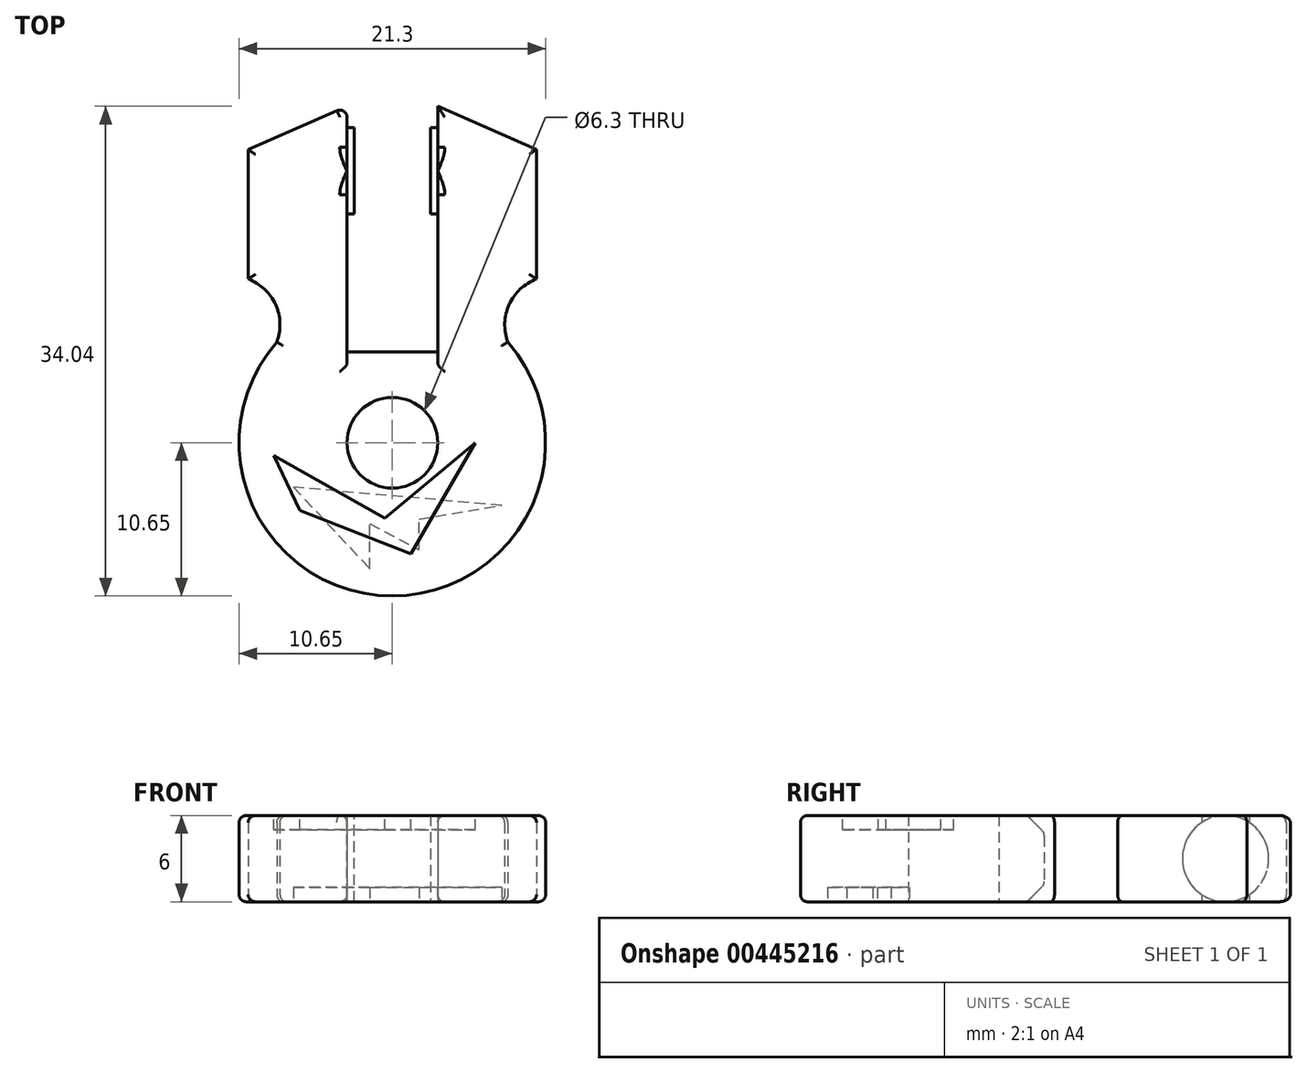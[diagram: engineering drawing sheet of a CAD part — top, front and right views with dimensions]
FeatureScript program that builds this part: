
annotation { "Feature Type Name" : "Feature", "Feature Type Description" : "" }
export const myFeature = defineFeature(function(context is Context, id is Id, definition is map)
    precondition{}
    {
        {
            var Q0;
            Q0=qCreatedBy(makeId("Top.planeOp"),FACE);
            var sketch = newSketch(context, id + "F0", { "sketchPlane" : qUnion([Q0])});
            skArc(sketch, "E0", {"start": v(-8.03, 7) * mm, "mid": v(0, -10.65) * mm, "end": v(8.03, 7) * mm});
            skCircle(sketch, "E1", {"center": v(0, 0) * mm, "radius": 3.15 * mm});
            skLineSegment(sketch, "E2", {"start": v(3.15, 10.17) * mm, "end": v(3.15, 23.39) * mm});
            skLineSegment(sketch, "E3", {"start": v(-3.15, 10.17) * mm, "end": v(-3.15, 23.39) * mm});
            skLineSegment(sketch, "E4", {"start": v(-3.15, 23.39) * mm, "end": v(-10.02, 20.38) * mm});
            skLineSegment(sketch, "E5.MirrorCS", {"start": v(3.15, 23.39) * mm, "end": v(10.02, 20.38) * mm});
            skLineSegment(sketch, "E6", {"start": v(-10.02, 20.38) * mm, "end": v(-10.02, 11.38) * mm});
            skLineSegment(sketch, "E7", {"start": v(10.02, 20.38) * mm, "end": v(10.02, 11.38) * mm});
            skLineSegment(sketch, "E8", {"start": v(-3.15, 23.39) * mm, "end": v(-3.15, 21.89) * mm});
            skLineSegment(sketch, "E9", {"start": v(-3.15, 21.89) * mm, "end": v(-2.65, 21.89) * mm});
            skLineSegment(sketch, "E10", {"start": v(-2.65, 21.89) * mm, "end": v(-2.65, 15.89) * mm});
            skLineSegment(sketch, "E11", {"start": v(-2.65, 15.89) * mm, "end": v(-3.15, 15.89) * mm});
            skLineSegment(sketch, "E12", {"start": v(-2.65, 18.89) * mm, "end": v(-3.15, 18.89) * mm});
            skLineSegment(sketch, "E13.MirrorCS", {"start": v(2.65, 21.89) * mm, "end": v(2.65, 15.89) * mm});
            skLineSegment(sketch, "E14.MirrorCS", {"start": v(2.65, 18.89) * mm, "end": v(3.15, 18.89) * mm});
            skLineSegment(sketch, "E15.MirrorCS", {"start": v(2.65, 15.89) * mm, "end": v(3.15, 15.89) * mm});
            skLineSegment(sketch, "E16.MirrorCS", {"start": v(3.15, 21.89) * mm, "end": v(2.65, 21.89) * mm});
            skPoint(sketch, "E17.orphan", {"position": v(6.63, 8.34) * mm});
            skArc(sketch, "E18.MirrorCS", {"start": v(-10.02, 11.38) * mm, "mid": v(-8.11, 9.6) * mm, "end": v(-8.03, 7) * mm});
            skPoint(sketch, "E19.orphan", {"position": v(-6.63, 8.34) * mm});
            skLineSegment(sketch, "E20", {"start": v(0, 6.3) * mm, "end": v(-3.15, 6.3) * mm});
            skLineSegment(sketch, "E21", {"start": v(-3.15, 6.3) * mm, "end": v(-3.15, 10.17) * mm});
            skLineSegment(sketch, "E22.MirrorCS", {"start": v(3.15, 6.3) * mm, "end": v(3.15, 10.17) * mm});
            skLineSegment(sketch, "E23.MirrorCS", {"start": v(0, 6.3) * mm, "end": v(3.15, 6.3) * mm});
            skArc(sketch, "E24.MirrorCS", {"start": v(10.02, 11.38) * mm, "mid": v(8.11, 9.6) * mm, "end": v(8.03, 7) * mm});
            skSolve(sketch);
        }
        {
            var Q0;
            Q0=makeQuery(id+"F0.imprint","IMPRINT",FACE,{"disambiguationData":[TD([[makeQuery(id+"F0.imprint","IMPRINT",EDGE,{"derivedFrom":sQuery(id+"F0.wireOp",EDGE,"E1")}),-1.0]])]});
            extrude(context, id + "F1", {"entities" : qUnion([Q0]), "depth" : 3 * mm, "hasSecondDirection" : true, "secondDirectionOppositeDirection" : true, "secondDirectionDepth" : 3 * mm});
        }
        {
            var Q0;
            Q0=makeQuery(id+"F1.opExtrude","SWEPT_FACE",FACE,{"disambiguationData":[OSD([sQuery(id+"F0.wireOp",EDGE,"E3"),sQuery(id+"F0.wireOp",EDGE,"E8"),sQuery(id+"F0.wireOp",EDGE,"E21")])]});
            var sketch = newSketch(context, id + "F2", { "sketchPlane" : qUnion([Q0])});
            skPoint(sketch, "E25.endSnap0", {"position": v(23.39, 0) * mm});
            skCircle(sketch, "E26", {"center": v(18.89, 0) * mm, "radius": 3 * mm});
            skSolve(sketch);
        }
        {
            var Q0;
            {var subQ0=sQuery(id+"F2.wireOp",EDGE,"E26");var subQ1=sQuery(id+"F0.wireOp",EDGE,"E21");var subQ2=sQuery(id+"F0.wireOp",EDGE,"E8");var subQ3=sQuery(id+"F0.wireOp",EDGE,"E3");var subQ4=makeQuery(id+"F2.imprint","INTERSECT",VERTEX,{"derivedFrom":[makeQuery(id+"F1.opExtrude","CAP_EDGE",EDGE,{"disambiguationData":[OSD([subQ3,subQ2,subQ1])],"isStart":true}),subQ0]});Q0=makeQuery(id+"F2.imprint","IMPRINT",FACE,{"disambiguationData":[TD([[makeQuery(id+"F2.imprint","IMPRINT",EDGE,{"disambiguationData":[TD([[subQ4,1.0]])],"derivedFrom":subQ0}),1.0]])]});}
            extrude(context, id + "F3", {"entities" : qUnion([Q0]), "operationType" : NewBodyOperationType.ADD, "depth" : .5 * mm});
        }
        {
            var Q0;
            Q0=makeQuery(id+"F1.opExtrude","SWEPT_FACE",FACE,{"disambiguationData":[OSD([sQuery(id+"F0.wireOp",EDGE,"E2"),sQuery(id+"F0.wireOp",EDGE,"E22.MirrorCS")])]});
            var sketch = newSketch(context, id + "F4", { "sketchPlane" : qUnion([Q0])});
            skPoint(sketch, "E27.endSnap0", {"position": v(-23.39, 0) * mm});
            skCircle(sketch, "E28", {"center": v(-18.89, 0) * mm, "radius": 3 * mm});
            skSolve(sketch);
        }
        {
            var Q0;
            {var subQ0=sQuery(id+"F4.wireOp",EDGE,"E28");var subQ1=sQuery(id+"F0.wireOp",EDGE,"E22.MirrorCS");var subQ2=sQuery(id+"F0.wireOp",EDGE,"E2");var subQ3=makeQuery(id+"F4.imprint","INTERSECT",VERTEX,{"derivedFrom":[makeQuery(id+"F1.opExtrude","CAP_EDGE",EDGE,{"disambiguationData":[OSD([subQ2,subQ1])],"isStart":true}),subQ0]});Q0=makeQuery(id+"F4.imprint","IMPRINT",FACE,{"disambiguationData":[TD([[makeQuery(id+"F4.imprint","IMPRINT",EDGE,{"disambiguationData":[TD([[subQ3,1.0]])],"derivedFrom":subQ0}),1.0]])]});}
            extrude(context, id + "F5", {"entities" : qUnion([Q0]), "operationType" : NewBodyOperationType.ADD, "depth" : .5 * mm});
        }
        {
            var Q0;
            Q0=makeQuery(id+"F1.opExtrude","CAP_EDGE",EDGE,{"disambiguationData":[OSD([sQuery(id+"F0.wireOp",EDGE,"E20"),sQuery(id+"F0.wireOp",EDGE,"E23.MirrorCS")])],"isStart":false});
            var Q1;
            Q1=makeQuery(id+"F1.opExtrude","CAP_EDGE",EDGE,{"disambiguationData":[OSD([sQuery(id+"F0.wireOp",EDGE,"E20"),sQuery(id+"F0.wireOp",EDGE,"E23.MirrorCS")])],"isStart":true});
            chamfer(context, id + "F6", {"entities" : qUnion([Q0, Q1]), "width" : 1.2 * mm, "tangentPropagation" : true});
        }
        {
            var Q0;
            {var subQ0=sQuery(id+"F0.wireOp",EDGE,"E23.MirrorCS");var subQ1=sQuery(id+"F0.wireOp",EDGE,"E20");Q0=makeQuery(id+"F6.opChamfer","BLEND_EDGE",EDGE,{"blendedFrom":[makeQuery(id+"F1.opExtrude","CAP_EDGE",EDGE,{"disambiguationData":[OSD([subQ1,subQ0])],"isStart":false}),makeQuery(id+"F1.opExtrude","SWEPT_FACE",FACE,{"disambiguationData":[OSD([subQ1,subQ0])]})],"blendedInto":[makeQuery(id+"F1.opExtrude","SWEPT_FACE",FACE,{"disambiguationData":[OSD([subQ1,subQ0])]})]});}
            var Q1;
            {var subQ0=sQuery(id+"F0.wireOp",EDGE,"E23.MirrorCS");var subQ1=sQuery(id+"F0.wireOp",EDGE,"E20");Q1=makeQuery(id+"F6.opChamfer","BLEND_EDGE",EDGE,{"blendedFrom":[makeQuery(id+"F1.opExtrude","CAP_EDGE",EDGE,{"disambiguationData":[OSD([subQ1,subQ0])],"isStart":true}),makeQuery(id+"F1.opExtrude","SWEPT_FACE",FACE,{"disambiguationData":[OSD([subQ1,subQ0])]})],"blendedInto":[makeQuery(id+"F1.opExtrude","SWEPT_FACE",FACE,{"disambiguationData":[OSD([subQ1,subQ0])]})]});}
            fillet(context, id + "F7", {"entities" : qUnion([Q0, Q1]), "radius" : .5 * mm, "tangentPropagation" : true, "allowEdgeOverflow" : false});
        }
        {
            var Q0;
            {var subQ0=sQuery(id+"F0.wireOp",EDGE,"E23.MirrorCS");var subQ1=sQuery(id+"F0.wireOp",EDGE,"E20");Q0=makeQuery(id+"F6.opChamfer","BLEND_EDGE",EDGE,{"blendedFrom":[makeQuery(id+"F1.opExtrude","CAP_EDGE",EDGE,{"disambiguationData":[OSD([subQ1,subQ0])],"isStart":false}),makeQuery(id+"F1.opExtrude","CAP_FACE",FACE,{"disambiguationData":[OSD([sQuery(id+"F0.wireOp",EDGE,"E0"),sQuery(id+"F0.wireOp",EDGE,"E1"),sQuery(id+"F0.wireOp",EDGE,"E2"),sQuery(id+"F0.wireOp",EDGE,"E3"),sQuery(id+"F0.wireOp",EDGE,"E4"),sQuery(id+"F0.wireOp",EDGE,"E5.MirrorCS"),sQuery(id+"F0.wireOp",EDGE,"E6"),sQuery(id+"F0.wireOp",EDGE,"E7"),sQuery(id+"F0.wireOp",EDGE,"E8"),sQuery(id+"F0.wireOp",EDGE,"E18.MirrorCS"),subQ1,sQuery(id+"F0.wireOp",EDGE,"E21"),sQuery(id+"F0.wireOp",EDGE,"E22.MirrorCS"),subQ0,sQuery(id+"F0.wireOp",EDGE,"E24.MirrorCS")])],"isStart":false})],"blendedInto":[makeQuery(id+"F1.opExtrude","CAP_FACE",FACE,{"disambiguationData":[OSD([sQuery(id+"F0.wireOp",EDGE,"E0"),sQuery(id+"F0.wireOp",EDGE,"E1"),sQuery(id+"F0.wireOp",EDGE,"E2"),sQuery(id+"F0.wireOp",EDGE,"E3"),sQuery(id+"F0.wireOp",EDGE,"E4"),sQuery(id+"F0.wireOp",EDGE,"E5.MirrorCS"),sQuery(id+"F0.wireOp",EDGE,"E6"),sQuery(id+"F0.wireOp",EDGE,"E7"),sQuery(id+"F0.wireOp",EDGE,"E8"),sQuery(id+"F0.wireOp",EDGE,"E18.MirrorCS"),subQ1,sQuery(id+"F0.wireOp",EDGE,"E21"),sQuery(id+"F0.wireOp",EDGE,"E22.MirrorCS"),subQ0,sQuery(id+"F0.wireOp",EDGE,"E24.MirrorCS")])],"isStart":false})]});}
            var Q1;
            {var subQ0=sQuery(id+"F0.wireOp",EDGE,"E23.MirrorCS");var subQ1=sQuery(id+"F0.wireOp",EDGE,"E20");Q1=makeQuery(id+"F6.opChamfer","BLEND_EDGE",EDGE,{"blendedFrom":[makeQuery(id+"F1.opExtrude","CAP_EDGE",EDGE,{"disambiguationData":[OSD([subQ1,subQ0])],"isStart":true}),makeQuery(id+"F1.opExtrude","CAP_FACE",FACE,{"disambiguationData":[OSD([sQuery(id+"F0.wireOp",EDGE,"E0"),sQuery(id+"F0.wireOp",EDGE,"E1"),sQuery(id+"F0.wireOp",EDGE,"E2"),sQuery(id+"F0.wireOp",EDGE,"E3"),sQuery(id+"F0.wireOp",EDGE,"E4"),sQuery(id+"F0.wireOp",EDGE,"E5.MirrorCS"),sQuery(id+"F0.wireOp",EDGE,"E6"),sQuery(id+"F0.wireOp",EDGE,"E7"),sQuery(id+"F0.wireOp",EDGE,"E8"),sQuery(id+"F0.wireOp",EDGE,"E18.MirrorCS"),subQ1,sQuery(id+"F0.wireOp",EDGE,"E21"),sQuery(id+"F0.wireOp",EDGE,"E22.MirrorCS"),subQ0,sQuery(id+"F0.wireOp",EDGE,"E24.MirrorCS")])],"isStart":true})],"blendedInto":[makeQuery(id+"F1.opExtrude","CAP_FACE",FACE,{"disambiguationData":[OSD([sQuery(id+"F0.wireOp",EDGE,"E0"),sQuery(id+"F0.wireOp",EDGE,"E1"),sQuery(id+"F0.wireOp",EDGE,"E2"),sQuery(id+"F0.wireOp",EDGE,"E3"),sQuery(id+"F0.wireOp",EDGE,"E4"),sQuery(id+"F0.wireOp",EDGE,"E5.MirrorCS"),sQuery(id+"F0.wireOp",EDGE,"E6"),sQuery(id+"F0.wireOp",EDGE,"E7"),sQuery(id+"F0.wireOp",EDGE,"E8"),sQuery(id+"F0.wireOp",EDGE,"E18.MirrorCS"),subQ1,sQuery(id+"F0.wireOp",EDGE,"E21"),sQuery(id+"F0.wireOp",EDGE,"E22.MirrorCS"),subQ0,sQuery(id+"F0.wireOp",EDGE,"E24.MirrorCS")])],"isStart":true})]});}
            fillet(context, id + "F8", {"entities" : qUnion([Q0, Q1]), "radius" : .4 * mm, "tangentPropagation" : true, "allowEdgeOverflow" : false});
        }
        {
            var Q0;
            Q0=makeQuery(id+"F1.opExtrude","CAP_FACE",FACE,{"disambiguationData":[OSD([sQuery(id+"F0.wireOp",EDGE,"E0"),sQuery(id+"F0.wireOp",EDGE,"E1"),sQuery(id+"F0.wireOp",EDGE,"E2"),sQuery(id+"F0.wireOp",EDGE,"E3"),sQuery(id+"F0.wireOp",EDGE,"E4"),sQuery(id+"F0.wireOp",EDGE,"E5.MirrorCS"),sQuery(id+"F0.wireOp",EDGE,"E6"),sQuery(id+"F0.wireOp",EDGE,"E7"),sQuery(id+"F0.wireOp",EDGE,"E8"),sQuery(id+"F0.wireOp",EDGE,"E18.MirrorCS"),sQuery(id+"F0.wireOp",EDGE,"E20"),sQuery(id+"F0.wireOp",EDGE,"E21"),sQuery(id+"F0.wireOp",EDGE,"E22.MirrorCS"),sQuery(id+"F0.wireOp",EDGE,"E23.MirrorCS"),sQuery(id+"F0.wireOp",EDGE,"E24.MirrorCS")])],"isStart":false});
            var sketch = newSketch(context, id + "F9", { "sketchPlane" : qUnion([Q0])});
            skLineSegment(sketch, "E29", {"start": v(-8.23, -0.9) * mm, "end": v(-0.51, -5.24) * mm});
            skLineSegment(sketch, "E30", {"start": v(-0.51, -5.24) * mm, "end": v(5.75, 0) * mm});
            skLineSegment(sketch, "E31", {"start": v(5.75, 0) * mm, "end": v(1.3, -7.72) * mm});
            skLineSegment(sketch, "E32", {"start": v(1.3, -7.72) * mm, "end": v(-6.42, -4.7) * mm});
            skLineSegment(sketch, "E33", {"start": v(-6.42, -4.7) * mm, "end": v(-8.23, -0.9) * mm});
            skSolve(sketch);
        }
        {
            var Q0;
            Q0=makeQuery(id+"F9.imprint","IMPRINT",FACE,{"disambiguationData":[TD([[makeQuery(id+"F9.imprint","IMPRINT",EDGE,{"derivedFrom":sQuery(id+"F9.wireOp",EDGE,"E29")}),-1.0]])]});
            extrude(context, id + "F10", {"entities" : qUnion([Q0]), "operationType" : NewBodyOperationType.REMOVE, "oppositeDirection" : true, "depth" : 1 * mm});
        }
        {
            var Q0;
            Q0=makeQuery(id+"F1.opExtrude","CAP_FACE",FACE,{"disambiguationData":[OSD([sQuery(id+"F0.wireOp",EDGE,"E0"),sQuery(id+"F0.wireOp",EDGE,"E1"),sQuery(id+"F0.wireOp",EDGE,"E2"),sQuery(id+"F0.wireOp",EDGE,"E3"),sQuery(id+"F0.wireOp",EDGE,"E4"),sQuery(id+"F0.wireOp",EDGE,"E5.MirrorCS"),sQuery(id+"F0.wireOp",EDGE,"E6"),sQuery(id+"F0.wireOp",EDGE,"E7"),sQuery(id+"F0.wireOp",EDGE,"E8"),sQuery(id+"F0.wireOp",EDGE,"E18.MirrorCS"),sQuery(id+"F0.wireOp",EDGE,"E20"),sQuery(id+"F0.wireOp",EDGE,"E21"),sQuery(id+"F0.wireOp",EDGE,"E22.MirrorCS"),sQuery(id+"F0.wireOp",EDGE,"E23.MirrorCS"),sQuery(id+"F0.wireOp",EDGE,"E24.MirrorCS")])],"isStart":true});
            var sketch = newSketch(context, id + "F11", { "sketchPlane" : qUnion([Q0])});
            skLineSegment(sketch, "E34", {"start": v(-6.86, 3.09) * mm, "end": v(-1.56, 8.75) * mm});
            skLineSegment(sketch, "E35", {"start": v(-1.56, 8.75) * mm, "end": v(-1.56, 5.62) * mm});
            skLineSegment(sketch, "E36", {"start": v(-1.56, 5.62) * mm, "end": v(1.87, 7.43) * mm});
            skLineSegment(sketch, "E37", {"start": v(1.87, 7.43) * mm, "end": v(1.87, 5.32) * mm});
            skLineSegment(sketch, "E38", {"start": v(1.87, 5.32) * mm, "end": v(7.6, 4.36) * mm});
            skLineSegment(sketch, "E39", {"start": v(7.6, 4.36) * mm, "end": v(-6.86, 3.09) * mm});
            skSolve(sketch);
        }
        {
            var Q0;
            Q0=makeQuery(id+"F11.imprint","IMPRINT",FACE,{"disambiguationData":[TD([[makeQuery(id+"F11.imprint","IMPRINT",EDGE,{"derivedFrom":sQuery(id+"F11.wireOp",EDGE,"E34")}),-1.0]])]});
            extrude(context, id + "F12", {"entities" : qUnion([Q0]), "operationType" : NewBodyOperationType.REMOVE, "oppositeDirection" : true, "depth" : 1 * mm});
        }
        {
            var Q0;
            Q0=makeQuery(id+"F1.opExtrude","CAP_EDGE",EDGE,{"disambiguationData":[OSD([sQuery(id+"F0.wireOp",EDGE,"E4")])],"isStart":false});
            var Q1;
            Q1=makeQuery(id+"F1.opExtrude","CAP_EDGE",EDGE,{"disambiguationData":[OSD([sQuery(id+"F0.wireOp",EDGE,"E6")])],"isStart":false});
            var Q2;
            Q2=makeQuery(id+"F1.opExtrude","CAP_EDGE",EDGE,{"disambiguationData":[OSD([sQuery(id+"F0.wireOp",EDGE,"E18.MirrorCS")])],"isStart":false});
            var Q3;
            Q3=makeQuery(id+"F1.opExtrude","CAP_EDGE",EDGE,{"disambiguationData":[OSD([sQuery(id+"F0.wireOp",EDGE,"E0")])],"isStart":false});
            var Q4;
            Q4=makeQuery(id+"F1.opExtrude","CAP_EDGE",EDGE,{"disambiguationData":[OSD([sQuery(id+"F0.wireOp",EDGE,"E24.MirrorCS")])],"isStart":false});
            var Q5;
            Q5=makeQuery(id+"F1.opExtrude","CAP_EDGE",EDGE,{"disambiguationData":[OSD([sQuery(id+"F0.wireOp",EDGE,"E7")])],"isStart":false});
            var Q6;
            Q6=makeQuery(id+"F1.opExtrude","CAP_EDGE",EDGE,{"disambiguationData":[OSD([sQuery(id+"F0.wireOp",EDGE,"E5.MirrorCS")])],"isStart":false});
            var Q7;
            {var subQ0=sQuery(id+"F0.wireOp",EDGE,"E23.MirrorCS");var subQ1=sQuery(id+"F0.wireOp",EDGE,"E22.MirrorCS");var subQ2=sQuery(id+"F0.wireOp",EDGE,"E20");var subQ3=sQuery(id+"F0.wireOp",EDGE,"E2");Q7=makeQuery(id+"F5.boolean.opBoolean","SPLIT",EDGE,{"disambiguationData":[TD([makeQuery(id+"F1.opExtrude","SWEPT_FACE",FACE,{"disambiguationData":[OSD([subQ2,subQ0])]})])],"derivedFrom":makeQuery(id+"F1.opExtrude","CAP_EDGE",EDGE,{"disambiguationData":[OSD([subQ3,subQ1])],"isStart":false})});}
            fillet(context, id + "F13", {"entities" : qUnion([Q0, Q1, Q2, Q3, Q4, Q5, Q6, Q7]), "radius" : .5 * mm, "tangentPropagation" : true, "allowEdgeOverflow" : false});
        }
        {
            var Q0;
            Q0=makeQuery(id+"F1.opExtrude","CAP_EDGE",EDGE,{"disambiguationData":[OSD([sQuery(id+"F0.wireOp",EDGE,"E0")])],"isStart":true});
            var Q1;
            Q1=makeQuery(id+"F1.opExtrude","CAP_EDGE",EDGE,{"disambiguationData":[OSD([sQuery(id+"F0.wireOp",EDGE,"E18.MirrorCS")])],"isStart":true});
            var Q2;
            Q2=makeQuery(id+"F1.opExtrude","CAP_EDGE",EDGE,{"disambiguationData":[OSD([sQuery(id+"F0.wireOp",EDGE,"E6")])],"isStart":true});
            var Q3;
            Q3=makeQuery(id+"F1.opExtrude","CAP_EDGE",EDGE,{"disambiguationData":[OSD([sQuery(id+"F0.wireOp",EDGE,"E4")])],"isStart":true});
            var Q4;
            {var subQ0=sQuery(id+"F0.wireOp",EDGE,"E21");var subQ1=sQuery(id+"F0.wireOp",EDGE,"E8");var subQ2=sQuery(id+"F0.wireOp",EDGE,"E4");var subQ3=sQuery(id+"F0.wireOp",EDGE,"E3");Q4=makeQuery(id+"F3.boolean.opBoolean","SPLIT",EDGE,{"disambiguationData":[TD([makeQuery(id+"F1.opExtrude","SWEPT_FACE",FACE,{"disambiguationData":[OSD([subQ2])]})])],"derivedFrom":makeQuery(id+"F1.opExtrude","CAP_EDGE",EDGE,{"disambiguationData":[OSD([subQ3,subQ1,subQ0])],"isStart":true})});}
            var Q5;
            {var subQ0=sQuery(id+"F0.wireOp",EDGE,"E23.MirrorCS");var subQ1=sQuery(id+"F0.wireOp",EDGE,"E21");var subQ2=sQuery(id+"F0.wireOp",EDGE,"E20");var subQ3=sQuery(id+"F0.wireOp",EDGE,"E8");var subQ4=sQuery(id+"F0.wireOp",EDGE,"E3");Q5=makeQuery(id+"F3.boolean.opBoolean","SPLIT",EDGE,{"disambiguationData":[TD([makeQuery(id+"F1.opExtrude","SWEPT_FACE",FACE,{"disambiguationData":[OSD([subQ2,subQ0])]})])],"derivedFrom":makeQuery(id+"F1.opExtrude","CAP_EDGE",EDGE,{"disambiguationData":[OSD([subQ4,subQ3,subQ1])],"isStart":true})});}
            var Q6;
            {var subQ0=sQuery(id+"F0.wireOp",EDGE,"E23.MirrorCS");var subQ1=sQuery(id+"F0.wireOp",EDGE,"E22.MirrorCS");var subQ2=sQuery(id+"F0.wireOp",EDGE,"E20");var subQ3=sQuery(id+"F0.wireOp",EDGE,"E2");Q6=makeQuery(id+"F5.boolean.opBoolean","SPLIT",EDGE,{"disambiguationData":[TD([makeQuery(id+"F1.opExtrude","SWEPT_FACE",FACE,{"disambiguationData":[OSD([subQ2,subQ0])]})])],"derivedFrom":makeQuery(id+"F1.opExtrude","CAP_EDGE",EDGE,{"disambiguationData":[OSD([subQ3,subQ1])],"isStart":true})});}
            var Q7;
            {var subQ0=sQuery(id+"F0.wireOp",EDGE,"E22.MirrorCS");var subQ1=sQuery(id+"F0.wireOp",EDGE,"E5.MirrorCS");var subQ2=sQuery(id+"F0.wireOp",EDGE,"E2");Q7=makeQuery(id+"F5.boolean.opBoolean","SPLIT",EDGE,{"disambiguationData":[TD([makeQuery(id+"F1.opExtrude","SWEPT_FACE",FACE,{"disambiguationData":[OSD([subQ1])]})])],"derivedFrom":makeQuery(id+"F1.opExtrude","CAP_EDGE",EDGE,{"disambiguationData":[OSD([subQ2,subQ0])],"isStart":true})});}
            var Q8;
            Q8=makeQuery(id+"F1.opExtrude","CAP_EDGE",EDGE,{"disambiguationData":[OSD([sQuery(id+"F0.wireOp",EDGE,"E5.MirrorCS")])],"isStart":true});
            var Q9;
            Q9=makeQuery(id+"F1.opExtrude","CAP_EDGE",EDGE,{"disambiguationData":[OSD([sQuery(id+"F0.wireOp",EDGE,"E7")])],"isStart":true});
            var Q10;
            Q10=makeQuery(id+"F1.opExtrude","CAP_EDGE",EDGE,{"disambiguationData":[OSD([sQuery(id+"F0.wireOp",EDGE,"E24.MirrorCS")])],"isStart":true});
            fillet(context, id + "F14", {"entities" : qUnion([Q0, Q1, Q2, Q3, Q4, Q5, Q6, Q7, Q8, Q9, Q10]), "radius" : .5 * mm, "tangentPropagation" : true, "allowEdgeOverflow" : false});
        }
        {
            var Q0;
            {var subQ0=sQuery(id+"F0.wireOp",EDGE,"E23.MirrorCS");var subQ1=sQuery(id+"F0.wireOp",EDGE,"E21");var subQ2=sQuery(id+"F0.wireOp",EDGE,"E20");var subQ3=sQuery(id+"F0.wireOp",EDGE,"E8");var subQ4=sQuery(id+"F0.wireOp",EDGE,"E3");Q0=makeQuery(id+"F3.boolean.opBoolean","SPLIT",EDGE,{"disambiguationData":[TD([makeQuery(id+"F1.opExtrude","SWEPT_FACE",FACE,{"disambiguationData":[OSD([subQ2,subQ0])]})])],"derivedFrom":makeQuery(id+"F1.opExtrude","CAP_EDGE",EDGE,{"disambiguationData":[OSD([subQ4,subQ3,subQ1])],"isStart":false})});}
            var Q1;
            {var subQ0=sQuery(id+"F0.wireOp",EDGE,"E21");var subQ1=sQuery(id+"F0.wireOp",EDGE,"E8");var subQ2=sQuery(id+"F0.wireOp",EDGE,"E4");var subQ3=sQuery(id+"F0.wireOp",EDGE,"E3");Q1=makeQuery(id+"F3.boolean.opBoolean","SPLIT",EDGE,{"disambiguationData":[TD([makeQuery(id+"F1.opExtrude","SWEPT_FACE",FACE,{"disambiguationData":[OSD([subQ2])]})])],"derivedFrom":makeQuery(id+"F1.opExtrude","CAP_EDGE",EDGE,{"disambiguationData":[OSD([subQ3,subQ1,subQ0])],"isStart":false})});}
            fillet(context, id + "F15", {"entities" : qUnion([Q0, Q1]), "radius" : .5 * mm, "tangentPropagation" : true, "allowEdgeOverflow" : false});
        }
    });
